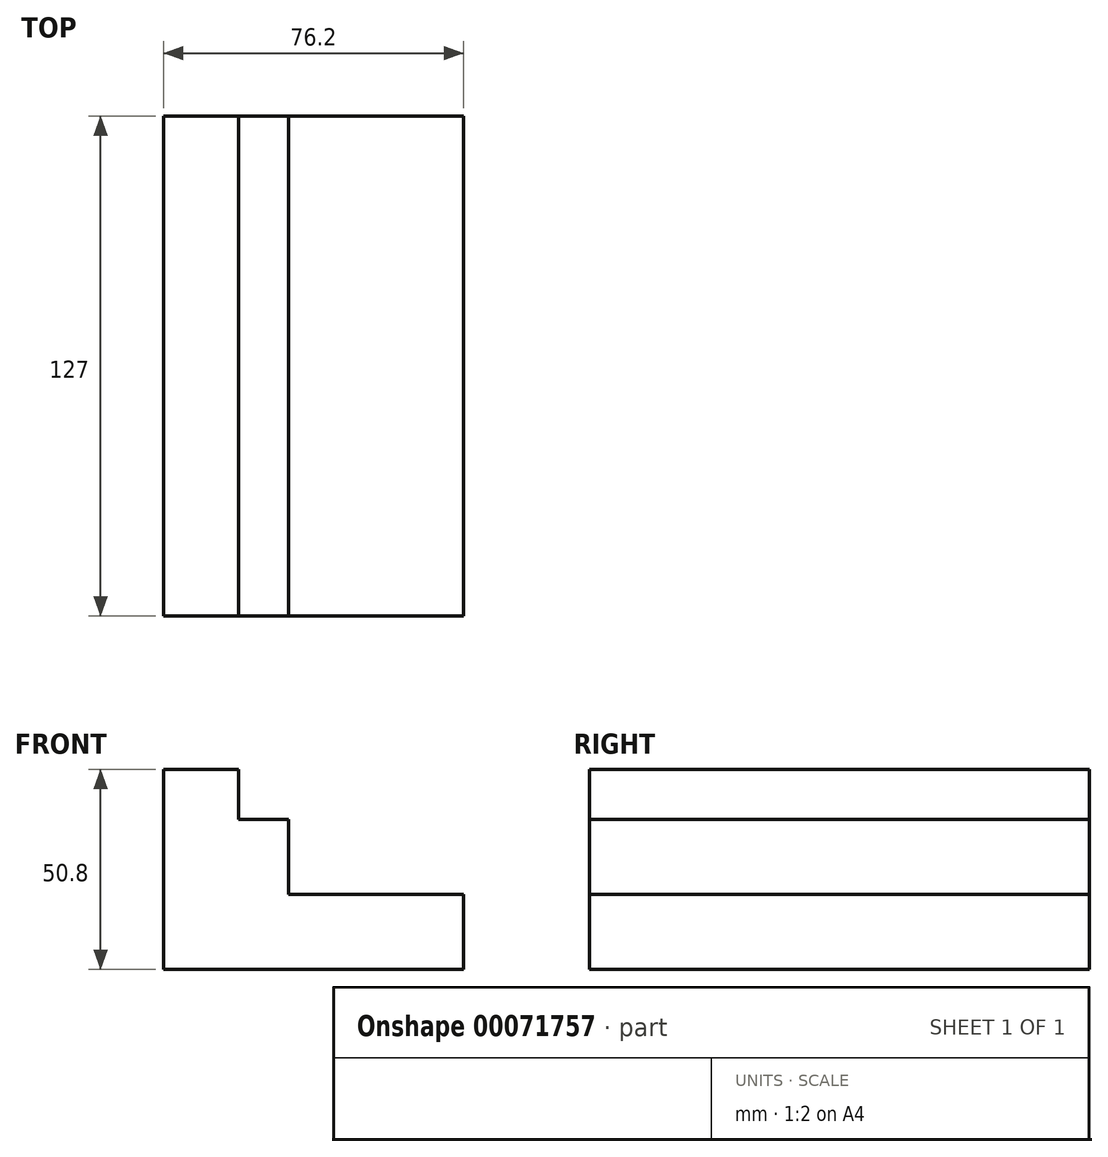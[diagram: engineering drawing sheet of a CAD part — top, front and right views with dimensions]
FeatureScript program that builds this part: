
annotation { "Feature Type Name" : "Feature", "Feature Type Description" : "" }
export const myFeature = defineFeature(function(context is Context, id is Id, definition is map)
    precondition{}
    {
        {
            var Q0;
            Q0=qCreatedBy(makeId("Front.planeOp"),FACE);
            var sketch = newSketch(context, id + "F0", { "sketchPlane" : qUnion([Q0])});
            skLineSegment(sketch, "E0", {"start": v(0, 0) * mm, "end": v(0, 50.8) * mm});
            skLineSegment(sketch, "E1", {"start": v(0, 50.8) * mm, "end": v(19.05, 50.8) * mm});
            skLineSegment(sketch, "E2", {"start": v(19.05, 50.8) * mm, "end": v(19.05, 38.1) * mm});
            skLineSegment(sketch, "E3", {"start": v(19.05, 38.1) * mm, "end": v(31.75, 38.1) * mm});
            skLineSegment(sketch, "E4", {"start": v(31.75, 38.1) * mm, "end": v(31.75, 19.05) * mm});
            skLineSegment(sketch, "E5", {"start": v(31.75, 19.05) * mm, "end": v(76.2, 19.05) * mm});
            skLineSegment(sketch, "E6", {"start": v(76.2, 19.05) * mm, "end": v(76.2, 0) * mm});
            skLineSegment(sketch, "E7", {"start": v(76.2, 0) * mm, "end": v(0, 0) * mm});
            skSolve(sketch);
        }
        {
            var Q0;
            Q0=makeQuery(id+"F0.imprint","IMPRINT",FACE,{"disambiguationData":[TD([[makeQuery(id+"F0.imprint","IMPRINT",EDGE,{"derivedFrom":sQuery(id+"F0.wireOp",EDGE,"E0")}),-1.0]])]});
            extrude(context, id + "F1", {"entities" : qUnion([Q0]), "depth" : 127 * mm});
        }
    });
